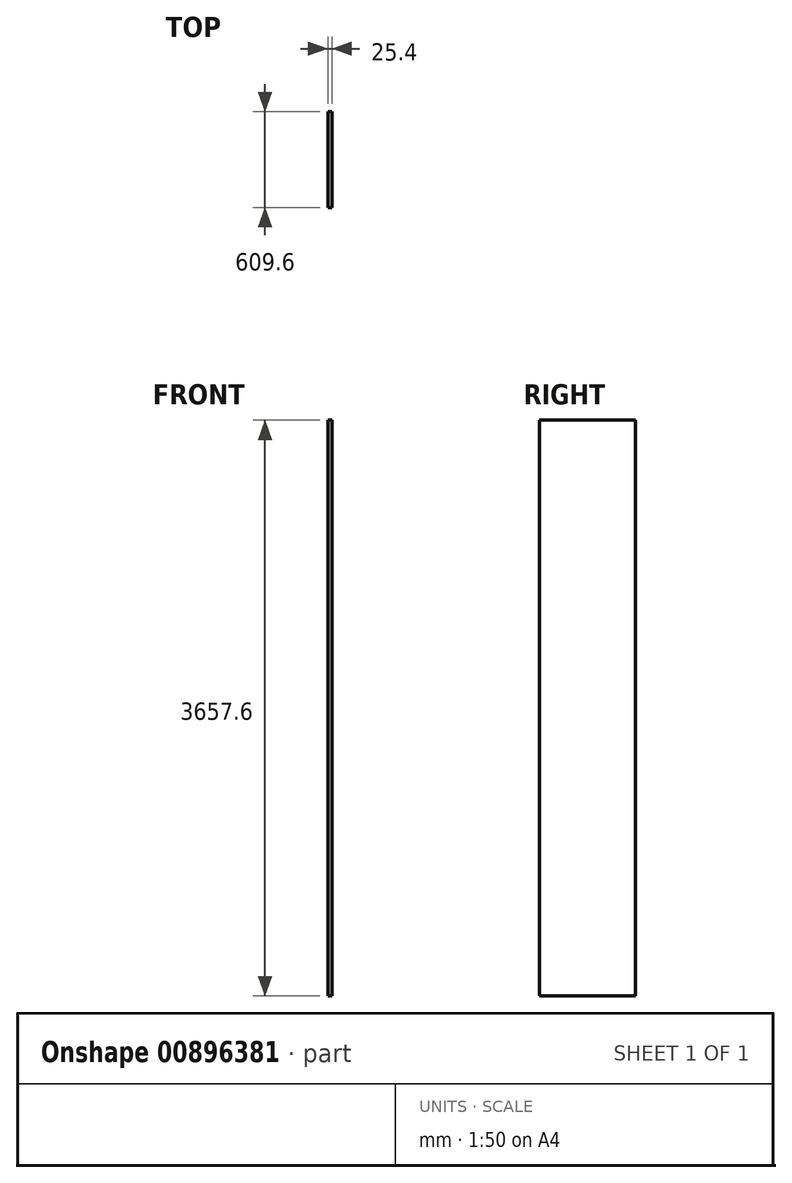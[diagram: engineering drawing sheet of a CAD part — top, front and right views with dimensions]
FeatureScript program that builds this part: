
annotation { "Feature Type Name" : "Feature", "Feature Type Description" : "" }
export const myFeature = defineFeature(function(context is Context, id is Id, definition is map)
    precondition{}
    {
        {
            var Q0;
            Q0=qCreatedBy(makeId("Right.planeOp"),FACE);
            var sketch = newSketch(context, id + "F0", { "sketchPlane" : qUnion([Q0])});
            skLineSegment(sketch, "E0.bottom", {"start": v(-609.6, 3657.6) * mm, "end": v(0, 3657.6) * mm});
            skLineSegment(sketch, "E0.top", {"start": v(-609.6, 0) * mm, "end": v(0, 0) * mm});
            skLineSegment(sketch, "E0.left", {"start": v(-609.6, 3657.6) * mm, "end": v(-609.6, 0) * mm});
            skLineSegment(sketch, "E0.right", {"start": v(0, 3657.6) * mm, "end": v(0, 0) * mm});
            skSolve(sketch);
        }
        {
            var Q0;
            Q0 = qSketchRegion(id + "F0", true);
            extrude(context, id + "F1", {"entities" : qUnion([Q0]), "depth" : 25.4 * mm, "offsetDistance" : 25.4 * mm});
        }
    });
